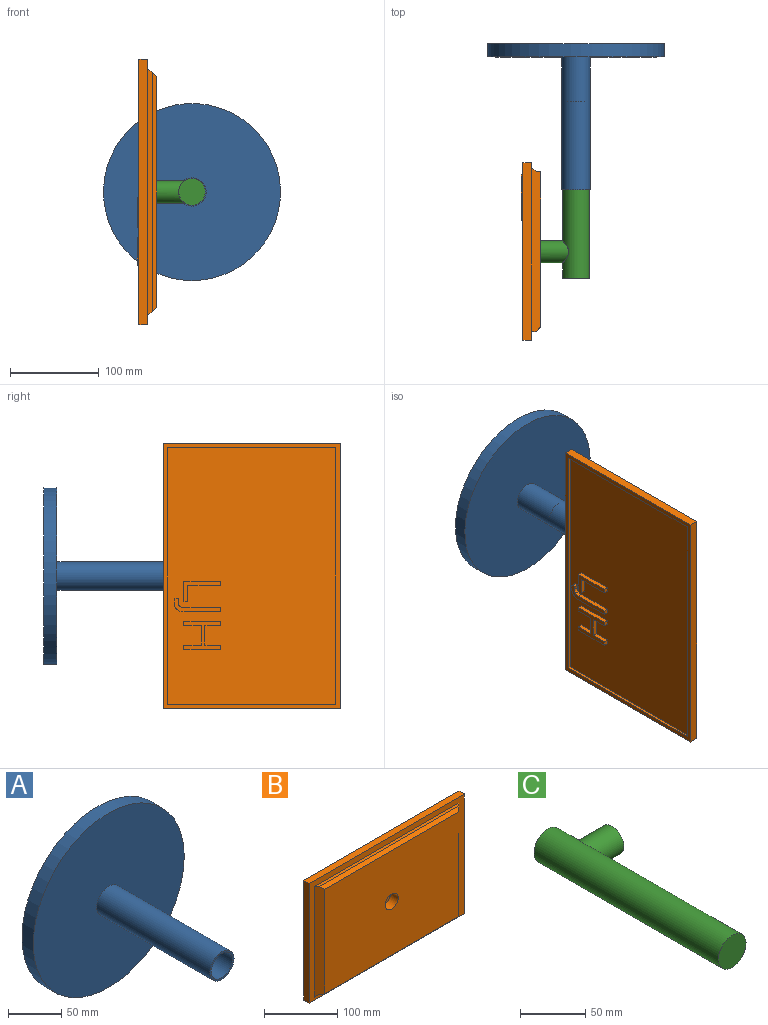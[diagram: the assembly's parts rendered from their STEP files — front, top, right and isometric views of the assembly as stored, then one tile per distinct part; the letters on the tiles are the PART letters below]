
ASSEMBLY  parts=3 mates=2
PART A: 9 faces, bbox 200x165x200 mm
  f0: cylinder r=100mm len=200mm, axis (0,1,0), area 9424.8mm2, adj f1,f2
  f1: plane 200x200mm, normal (0,-1,0), area 30611.7mm2, adj f0,f3
  f2: plane 200x200mm, normal (0,1,0), area 31415.9mm2, adj f0
  f3: cylinder r=16mm len=150mm, axis (0,1,0), area 15079.6mm2, adj f1,f4
  f4: plane 32x32mm, normal (0,-1,0), area 188.5mm2, adj f3,f8
  f5: cylinder r=98mm len=196mm, axis (0,1,0), area 6773.3mm2, adj f6,f7
  f6: plane 196x196mm, normal (0,1,0), area 29556.1mm2, adj f5,f8
  f7: plane 196x196mm, normal (0,-1,0), area 30171.9mm2, adj f5
  f8: cylinder r=14mm len=152mm, axis (0,1,0), area 13370.6mm2, adj f4,f6
PART B: 51 faces, bbox 300x22x200 mm
  f0: plane 300x10mm, normal (0,0,1), area 3000mm2, adj f1,f3,f4,f5
  f1: plane 200x10mm, normal (-1,0,0), area 2000mm2, adj f0,f2,f4,f5
  f2: plane 300x10mm, normal (0,0,-1), area 3000mm2, adj f1,f3,f4,f5
  f3: plane 200x10mm, normal (1,0,0), area 2000mm2, adj f0,f2,f4,f5
  f4: plane 300x200mm, normal (0,-1,0), area 8200mm2, adj f0,f1,f2,f3,f7,f9,f11,f12
  f5: plane 300x200mm, normal (0,1,0), area 4900mm2, adj f0,f1,f2,f3,f15,f16,f17,f18
  f6: plane 270x5mm, normal (0,0,-1), area 1325mm2, adj f8,f9,f11,f12
  f7: plane 280x5mm, normal (0,0,1), area 1375mm2, adj f4,f10,f11,f12
  f8: plane 260x175mm, normal (0,-1,0), area 45009.1mm2, adj f6,f10,f11,f12,f13
  f9: plane 280x5mm, normal (0,-0.71,-0.71), area 1944.5mm2, adj f4,f6,f11,f12
  f10: plane 270x5mm, normal (0,-0.71,0.71), area 1873.8mm2, adj f7,f8,f11,f12
  f11: plane 185x10mm, normal (0.71,-0.71,0), area 2545.6mm2, adj f4,f6,f7,f8,f9,f10
  f12: plane 185x10mm, normal (-0.71,-0.71,0), area 2545.6mm2, adj f4,f6,f7,f8,f9,f10
  f13: cylinder r=12.5mm len=25mm, axis (0,-1,0), area 1178.1mm2, adj f8,f14
  f14: plane 25x25mm, normal (0,-1,0), area 490.9mm2, adj f13
  f15: plane 190x3mm, normal (-1,0,0), area 570mm2, adj f5,f16,f18,f19
  f16: plane 290x3mm, normal (0,0,1), area 870mm2, adj f5,f15,f17,f19
  f17: plane 190x3mm, normal (1,0,0), area 570mm2, adj f5,f16,f18,f19
  f18: plane 290x3mm, normal (0,0,-1), area 870mm2, adj f5,f15,f17,f19
  f19: plane 290x190mm, normal (0,1,0), area 54047.2mm2, adj f15,f16,f17,f18,f20,f21,f22,f23
  f20: plane 23.1x5mm, normal (0,0,-1), area 115.5mm2, adj f19,f21,f25,f26
  f21: plane 5x4.36mm, normal (-1,0,0), area 21.8mm2, adj f19,f20,f22,f26
  f22: plane 18.29x5mm, normal (0,0,1), area 91.4mm2, adj f19,f21,f23,f26
  f23: plane 37.08x5mm, normal (-1,0,0), area 185.4mm2, adj f19,f22,f24,f26
  f24: plane 5x4.82mm, normal (0,0,1), area 24.1mm2, adj f19,f23,f25,f26
  f25: plane 41.44x5mm, normal (1,0,0), area 207.2mm2, adj f19,f20,f24,f26
  f26: plane 41.44x23.1mm, normal (0,1,0), area 279.4mm2, adj f20,f21,f22,f23,f24,f25
  f27: extruded ~7.83x5mm, area 43.1mm2, adj f19,f28,f36,f37
  f28: extruded ~8.35x5mm, area 45mm2, adj f19,f27,f29,f37
  f29: plane 41.04x5mm, normal (-1,0,0), area 205.2mm2, adj f19,f28,f30,f37
  f30: plane 5x4.82mm, normal (0,0,1), area 24.1mm2, adj f19,f29,f31,f37
  f31: plane 41.44x5mm, normal (1,0,0), area 207.2mm2, adj f19,f30,f32,f37
  f32: extruded ~5x4.9mm, area 26.1mm2, adj f19,f31,f33,f37
  f33: extruded ~5x4.27mm, area 23.8mm2, adj f19,f32,f34,f37
  f34: extruded ~5x4.19mm, area 21.2mm2, adj f19,f33,f35,f37
  f35: plane 5x4.11mm, normal (1,0,0), area 20.5mm2, adj f19,f34,f36,f37
  f36: extruded ~5x4.19mm, area 21.5mm2, adj f19,f27,f35,f37
  f37: plane 52.35x14.74mm, normal (0,1,0), area 280.2mm2, adj f27,f28,f29,f30,f31,f32,f33,f34
  f38: plane 41.44x5mm, normal (-1,0,0), area 207.2mm2, adj f19,f39,f49,f50
  f39: plane 5x4.82mm, normal (0,0,1), area 24.1mm2, adj f19,f38,f40,f50
  f40: plane 17.63x5mm, normal (1,0,0), area 88.2mm2, adj f19,f39,f41,f50
  f41: plane 21.83x5mm, normal (0,0,1), area 109.2mm2, adj f19,f40,f42,f50
  f42: plane 17.63x5mm, normal (-1,0,0), area 88.2mm2, adj f19,f41,f43,f50
  f43: plane 5x4.82mm, normal (0,0,1), area 24.1mm2, adj f19,f42,f44,f50
  f44: plane 41.44x5mm, normal (1,0,0), area 207.2mm2, adj f19,f43,f45,f50
  f45: plane 5x4.82mm, normal (0,0,-1), area 24.1mm2, adj f19,f44,f46,f50
  f46: plane 19.5x5mm, normal (-1,0,0), area 97.5mm2, adj f19,f45,f47,f50
  f47: plane 21.83x5mm, normal (0,0,-1), area 109.2mm2, adj f19,f46,f48,f50
  f48: plane 19.5x5mm, normal (1,0,0), area 97.5mm2, adj f19,f47,f49,f50
  f49: plane 5x4.82mm, normal (0,0,-1), area 24.1mm2, adj f19,f38,f48,f50
  f50: plane 41.44x31.46mm, normal (0,1,0), area 493.2mm2, adj f38,f39,f40,f41,f42,f43,f44,f45
PART C: 5 faces, bbox 55x200x30 mm
  f0: cylinder r=15mm len=200mm, axis (0,1,0), area 18298.4mm2, adj f1,f2,f3
  f1: plane 30x30mm, normal (0,-1,0), area 706.9mm2, adj f0
  f2: plane 30x30mm, normal (0,1,0), area 706.9mm2, adj f0
  f3: cylinder r=12.5mm len=31.71mm, axis (-1,0,0), area 2207.5mm2, adj f0,f4
  f4: plane 25x25mm, normal (1,0,0), area 490.9mm2, adj f3
PLACE A t=(-24.84,719.41,838.14)mm
PLACE B rot(axis=(0.58,-0.58,0.58),120deg) t=(-84.84,484.41,838.14)mm
PLACE C rot(axis=(0,0,1),180deg) t=(-24.84,454.41,838.14)mm
MATE revolute B.f13 <-> C.f3  axis (1,0,0) through (-64.84,484.41,838.14)mm
MATE slider C.f0 <-> A.f3  axis (0,-1,0) through (-24.84,554.41,838.14)mm
